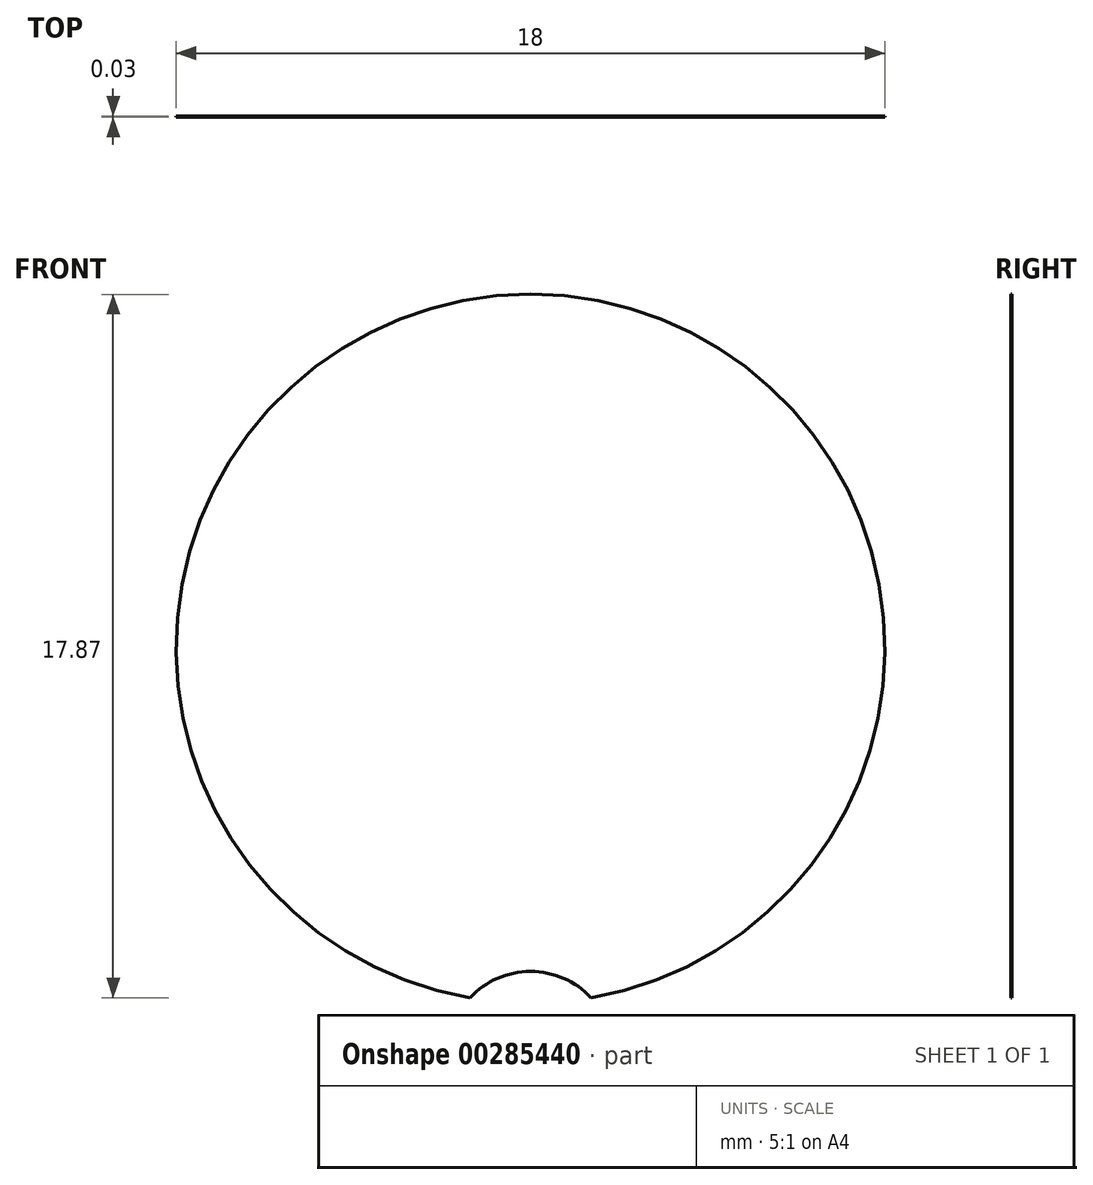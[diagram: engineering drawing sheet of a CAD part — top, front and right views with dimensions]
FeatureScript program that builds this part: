
annotation { "Feature Type Name" : "Feature", "Feature Type Description" : "" }
export const myFeature = defineFeature(function(context is Context, id is Id, definition is map)
    precondition{}
    {
        {
            var Q0;
            Q0=qCreatedBy(makeId("Front.planeOp"),FACE);
            var sketch = newSketch(context, id + "F0", { "sketchPlane" : qUnion([Q0])});
            skArc(sketch, "E0", {"start": v(1.54, -8.87) * mm, "mid": v(0, 9) * mm, "end": v(-1.54, -8.87) * mm});
            skArc(sketch, "E1", {"start": v(1.54, -8.87) * mm, "mid": v(0, -8.2) * mm, "end": v(-1.54, -8.87) * mm});
            skSolve(sketch);
        }
        {
            var Q0;
            Q0 = qSketchRegion(id + "F0", true);
            extrude(context, id + "F1", {"entities" : qUnion([Q0]), "depth" : 0.03 * mm});
        }
    });
